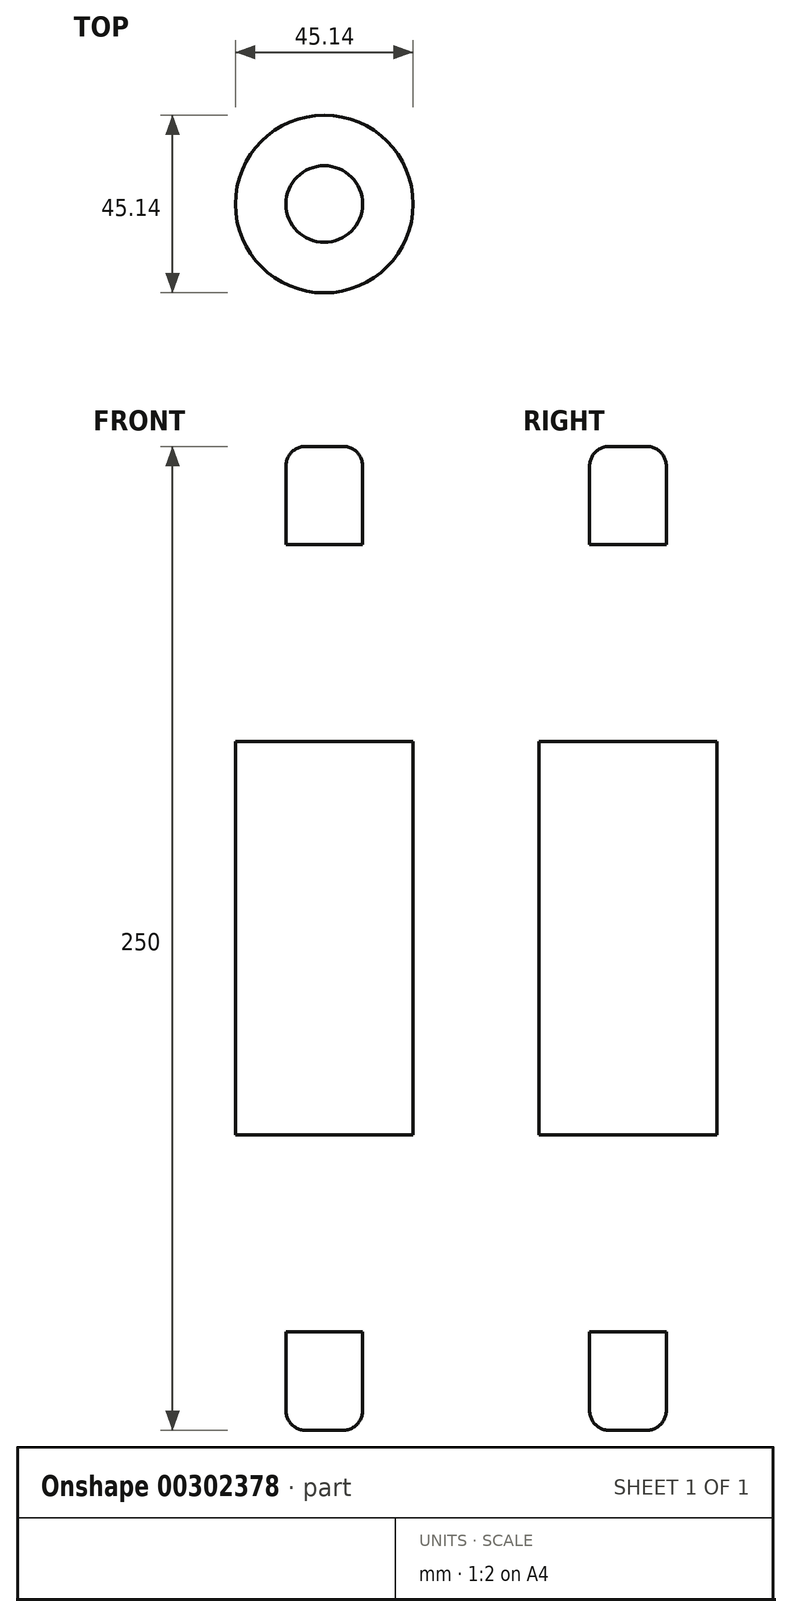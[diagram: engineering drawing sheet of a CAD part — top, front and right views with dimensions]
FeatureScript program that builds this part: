
annotation { "Feature Type Name" : "Feature", "Feature Type Description" : "" }
export const myFeature = defineFeature(function(context is Context, id is Id, definition is map)
    precondition{}
    {
        {
            var Q0;
            Q0=qCreatedBy(makeId("Top.planeOp"),FACE);
            var sketch = newSketch(context, id + "F0", { "sketchPlane" : qUnion([Q0])});
            skCircle(sketch, "E0", {"center": v(0, 0) * mm, "radius": 22.57 * mm});
            skSolve(sketch);
        }
        {
            var Q0;
            Q0=makeQuery(id+"F0.imprint","IMPRINT",FACE,{"disambiguationData":[TD([[makeQuery(id+"F0.imprint","IMPRINT",EDGE,{"derivedFrom":sQuery(id+"F0.wireOp",EDGE,"E0")}),1.0]])]});
            extrude(context, id + "F1", {"entities" : qUnion([Q0]), "depth" : 100 * mm});
        }
        {
            var Q0;
            Q0=makeQuery(id+"F1.opExtrude","CAP_FACE",FACE,{"disambiguationData":[OSD([sQuery(id+"F0.wireOp",EDGE,"E0")])],"isStart":false});
            var sketch = newSketch(context, id + "F2", { "sketchPlane" : qUnion([Q0])});
            skCircle(sketch, "E1", {"center": v(0, 0) * mm, "radius": 5 * mm});
            skSolve(sketch);
        }
        {
            var Q0;
            Q0=sQuery(id+"F2.wireOp",EDGE,"E1");
            extrude(context, id + "F3", {"bodyType" : ToolBodyType.SURFACE, "surfaceEntities" : qUnion([Q0]), "depth" : 50 * mm});
        }
        {
            var Q0;
            Q0=qCreatedBy(makeId("Top.planeOp"),FACE);
            cPlane(context, id + "F4", {"entities" : qUnion([Q0]), "cplaneType" : CPlaneType.OFFSET, "offset" : 50 * mm, "width" : 150 * mm, "height" : 150 * mm});
        }
        {
            var Q0;
            Q0=makeQuery(id+"F3.opExtrude","SWEPT_BODY",BODY,{"disambiguationData":[OSD([sQuery(id+"F2.wireOp",EDGE,"E1")])]});
            var Q1;
            Q1=qCreatedBy(id+"F4.planeOp",FACE);
            mirror(context, id + "F5", {"entities" : qUnion([Q0]), "mirrorPlane" : qUnion([Q1])});
        }
        {
            var Q0;
            Q0=qCreatedBy(id+"F4.planeOp",FACE);
            cPlane(context, id + "F6", {"entities" : qUnion([Q0]), "cplaneType" : CPlaneType.OFFSET, "offset" : 100 * mm, "width" : 150 * mm, "height" : 150 * mm});
        }
        {
            var Q0;
            Q0=qCreatedBy(id+"F6.planeOp",FACE);
            var sketch = newSketch(context, id + "F7", { "sketchPlane" : qUnion([Q0])});
            skCircle(sketch, "E2", {"center": v(0, 0) * mm, "radius": 9.74 * mm});
            skSolve(sketch);
        }
        {
            var Q0;
            Q0=makeQuery(id+"F7.imprint","IMPRINT",FACE,{"disambiguationData":[TD([[makeQuery(id+"F7.imprint","IMPRINT",EDGE,{"derivedFrom":sQuery(id+"F7.wireOp",EDGE,"E2")}),1.0]])]});
            extrude(context, id + "F8", {"entities" : qUnion([Q0]), "depth" : 25 * mm});
        }
        {
            var Q0;
            Q0=makeQuery(id+"F8.opExtrude","CAP_EDGE",EDGE,{"disambiguationData":[OSD([sQuery(id+"F7.wireOp",EDGE,"E2")])],"isStart":false});
            fillet(context, id + "F9", {"entities" : qUnion([Q0]), "radius" : 5 * mm, "tangentPropagation" : true, "allowEdgeOverflow" : false});
        }
        {
            var Q0;
            Q0=makeQuery(id+"F8.opExtrude","SWEPT_BODY",BODY,{"disambiguationData":[OSD([sQuery(id+"F7.wireOp",EDGE,"E2")])]});
            var Q1;
            Q1=qCreatedBy(id+"F4.planeOp",FACE);
            mirror(context, id + "F10", {"entities" : qUnion([Q0]), "mirrorPlane" : qUnion([Q1])});
        }
    });
